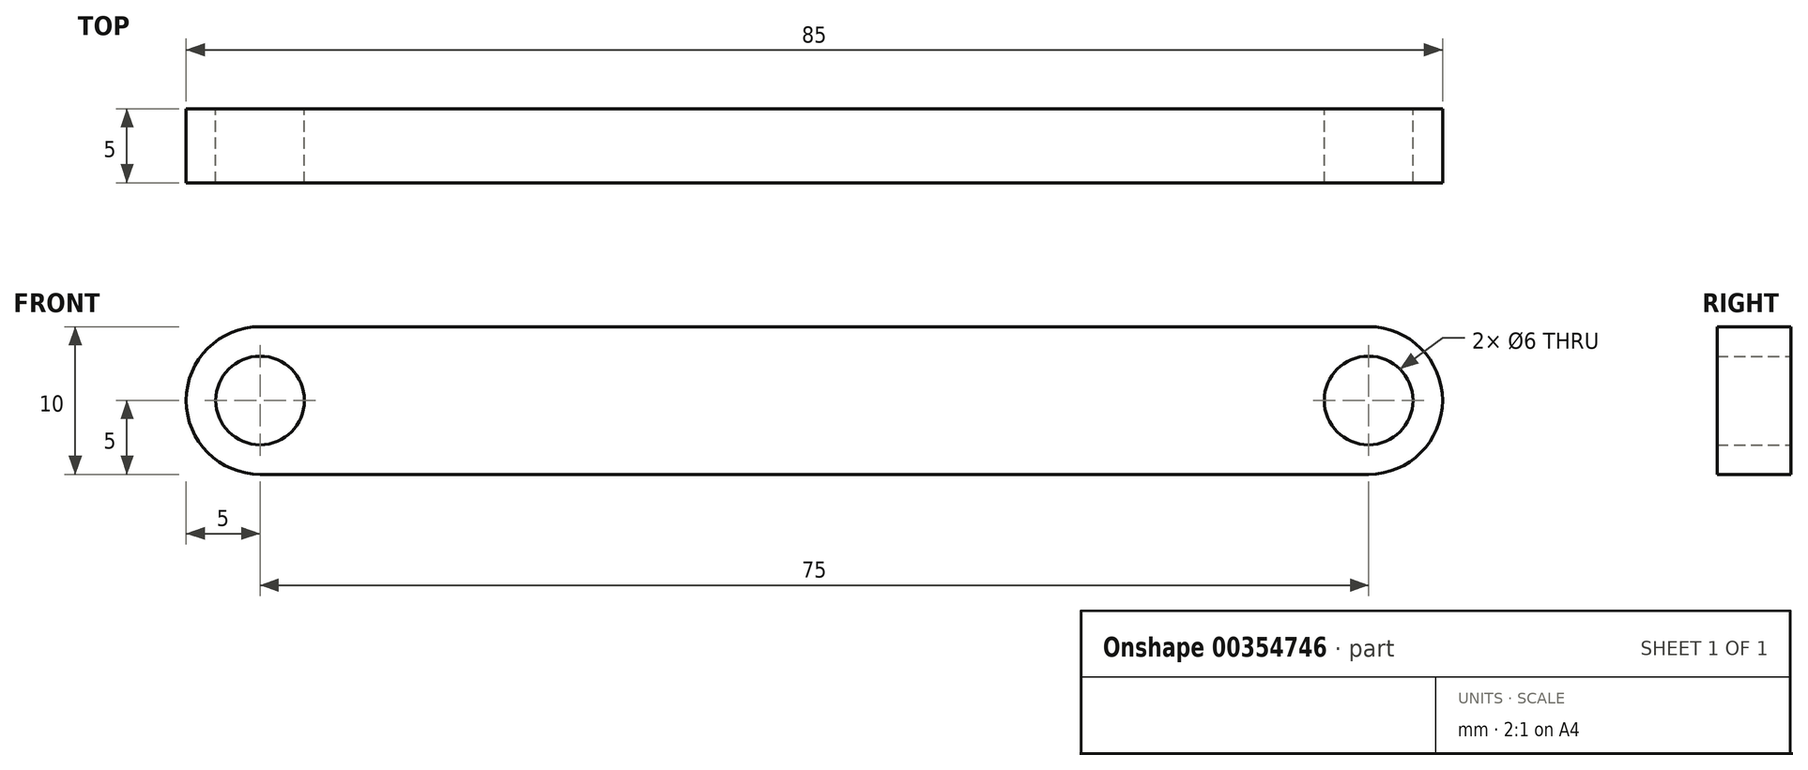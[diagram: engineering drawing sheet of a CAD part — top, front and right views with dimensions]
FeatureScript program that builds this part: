
annotation { "Feature Type Name" : "Feature", "Feature Type Description" : "" }
export const myFeature = defineFeature(function(context is Context, id is Id, definition is map)
    precondition{}
    {
        {
            var Q0;
            Q0=qCreatedBy(makeId("Front.planeOp"),FACE);
            var sketch = newSketch(context, id + "F0", { "sketchPlane" : qUnion([Q0])});
            skLineSegment(sketch, "E0.bottom", {"start": v(37.5, 5) * mm, "end": v(-37.5, 5) * mm});
            skLineSegment(sketch, "E0.top", {"start": v(37.5, -5) * mm, "end": v(-37.5, -5) * mm});
            skLineSegment(sketch, "E0.left", {"start": v(42.5, 0) * mm, "end": v(42.5, 0) * mm});
            skLineSegment(sketch, "E0.right", {"start": v(-42.5, 0) * mm, "end": v(-42.5, 0) * mm});
            skPoint(sketch, "E0.middle", {"position": v(0, 0) * mm});
            skPoint(sketch, "E1.endSnap0", {"position": v(-42.5, 0) * mm});
            skPoint(sketch, "E2.endSnap0", {"position": v(42.5, 0) * mm});
            skCircle(sketch, "E3", {"center": v(-37.5, 0) * mm, "radius": 3 * mm});
            skCircle(sketch, "E4", {"center": v(37.5, 0) * mm, "radius": 3 * mm});
            skPoint(sketch, "E5.visualSharp", {"position": v(-42.5, 5) * mm});
            skArc(sketch, "E5.filletArc", {"start": v(-37.5, 5) * mm, "mid": v(-41.04, 3.54) * mm, "end": v(-42.5, 0) * mm});
            skPoint(sketch, "E6.visualSharp", {"position": v(-42.5, -5) * mm});
            skArc(sketch, "E6.filletArc", {"start": v(-42.5, 0) * mm, "mid": v(-41.04, -3.54) * mm, "end": v(-37.5, -5) * mm});
            skPoint(sketch, "E7.visualSharp", {"position": v(42.5, -5) * mm});
            skArc(sketch, "E7.filletArc", {"start": v(37.5, -5) * mm, "mid": v(41.04, -3.54) * mm, "end": v(42.5, 0) * mm});
            skPoint(sketch, "E8.visualSharp", {"position": v(42.5, 5) * mm});
            skArc(sketch, "E8.filletArc", {"start": v(42.5, 0) * mm, "mid": v(41.04, 3.54) * mm, "end": v(37.5, 5) * mm});
            skSolve(sketch);
        }
        {
            var Q0;
            Q0=makeQuery(id+"F0.imprint","IMPRINT",FACE,{"disambiguationData":[TD([[makeQuery(id+"F0.imprint","IMPRINT",EDGE,{"derivedFrom":sQuery(id+"F0.wireOp",EDGE,"E0.bottom")}),1.0]])]});
            var Q1;
            Q1 = qConstructionFilter(qBodyType(qCreatedBy(id + "F0" ,EDGE), BodyType.WIRE), ConstructionObject.NO);
            extrude(context, id + "F1", {"entities" : qUnion([Q0]), "surfaceEntities" : qUnion([Q1]), "depth" : 5 * mm});
        }
    });
